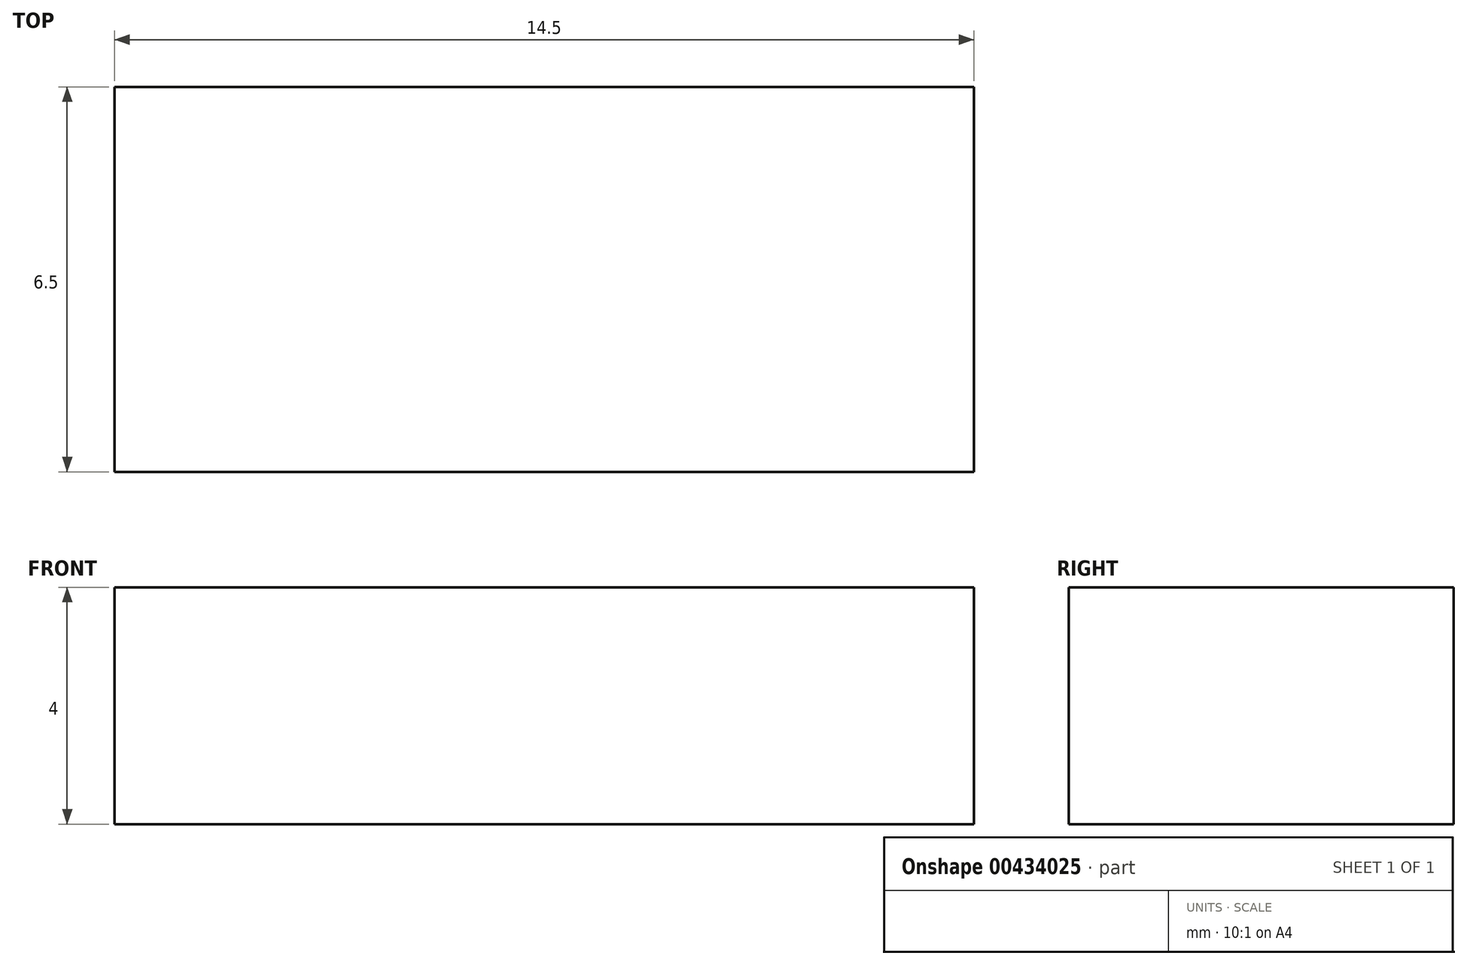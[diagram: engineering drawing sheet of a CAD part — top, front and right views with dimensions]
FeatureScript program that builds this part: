
annotation { "Feature Type Name" : "Feature", "Feature Type Description" : "" }
export const myFeature = defineFeature(function(context is Context, id is Id, definition is map)
    precondition{}
    {
        {
            var Q0;
            Q0=qCreatedBy(makeId("Front.planeOp"),FACE);
            var sketch = newSketch(context, id + "F0", { "sketchPlane" : qUnion([Q0])});
            skLineSegment(sketch, "E0.bottom", {"start": v(-7.25, 2) * mm, "end": v(7.25, 2) * mm});
            skLineSegment(sketch, "E0.top", {"start": v(-7.25, -2) * mm, "end": v(7.25, -2) * mm});
            skLineSegment(sketch, "E0.left", {"start": v(-7.25, 2) * mm, "end": v(-7.25, -2) * mm});
            skLineSegment(sketch, "E0.right", {"start": v(7.25, 2) * mm, "end": v(7.25, -2) * mm});
            skPoint(sketch, "E0.middle", {"position": v(0, 0) * mm});
            skLineSegment(sketch, "E1.bottom", {"start": v(-7.25, 2) * mm, "end": v(-3.25, 2) * mm});
            skLineSegment(sketch, "E1.top", {"start": v(-7.25, 9) * mm, "end": v(-3.25, 9) * mm});
            skLineSegment(sketch, "E1.left", {"start": v(-7.25, 2) * mm, "end": v(-7.25, 9) * mm});
            skLineSegment(sketch, "E1.right", {"start": v(-3.25, 2) * mm, "end": v(-3.25, 9) * mm});
            skLineSegment(sketch, "E2.bottom", {"start": v(7.25, 2) * mm, "end": v(3.25, 2) * mm});
            skLineSegment(sketch, "E2.top", {"start": v(7.25, 9) * mm, "end": v(3.25, 9) * mm});
            skLineSegment(sketch, "E2.left", {"start": v(7.25, 2) * mm, "end": v(7.25, 9) * mm});
            skLineSegment(sketch, "E2.right", {"start": v(3.25, 2) * mm, "end": v(3.25, 9) * mm});
            skSolve(sketch);
        }
        {
            var Q0;
            Q0=makeQuery(id+"F0.imprint","IMPRINT",FACE,{"disambiguationData":[TD([[makeQuery(id+"F0.imprint","IMPRINT",EDGE,{"derivedFrom":sQuery(id+"F0.wireOp",EDGE,"E1.bottom")}),1.0]])]});
            var Q1;
            Q1=makeQuery(id+"F0.imprint","IMPRINT",FACE,{"disambiguationData":[TD([[makeQuery(id+"F0.imprint","IMPRINT",EDGE,{"derivedFrom":sQuery(id+"F0.wireOp",EDGE,"E0.bottom")}),-1.0]])]});
            var Q2;
            Q2=makeQuery(id+"F0.imprint","IMPRINT",FACE,{"disambiguationData":[TD([[makeQuery(id+"F0.imprint","IMPRINT",EDGE,{"derivedFrom":sQuery(id+"F0.wireOp",EDGE,"E2.bottom")}),-1.0]])]});
            extrude(context, id + "F1", {"entities" : qUnion([Q0, Q1, Q2]), "depth" : 6.5 * mm});
        }
    });
